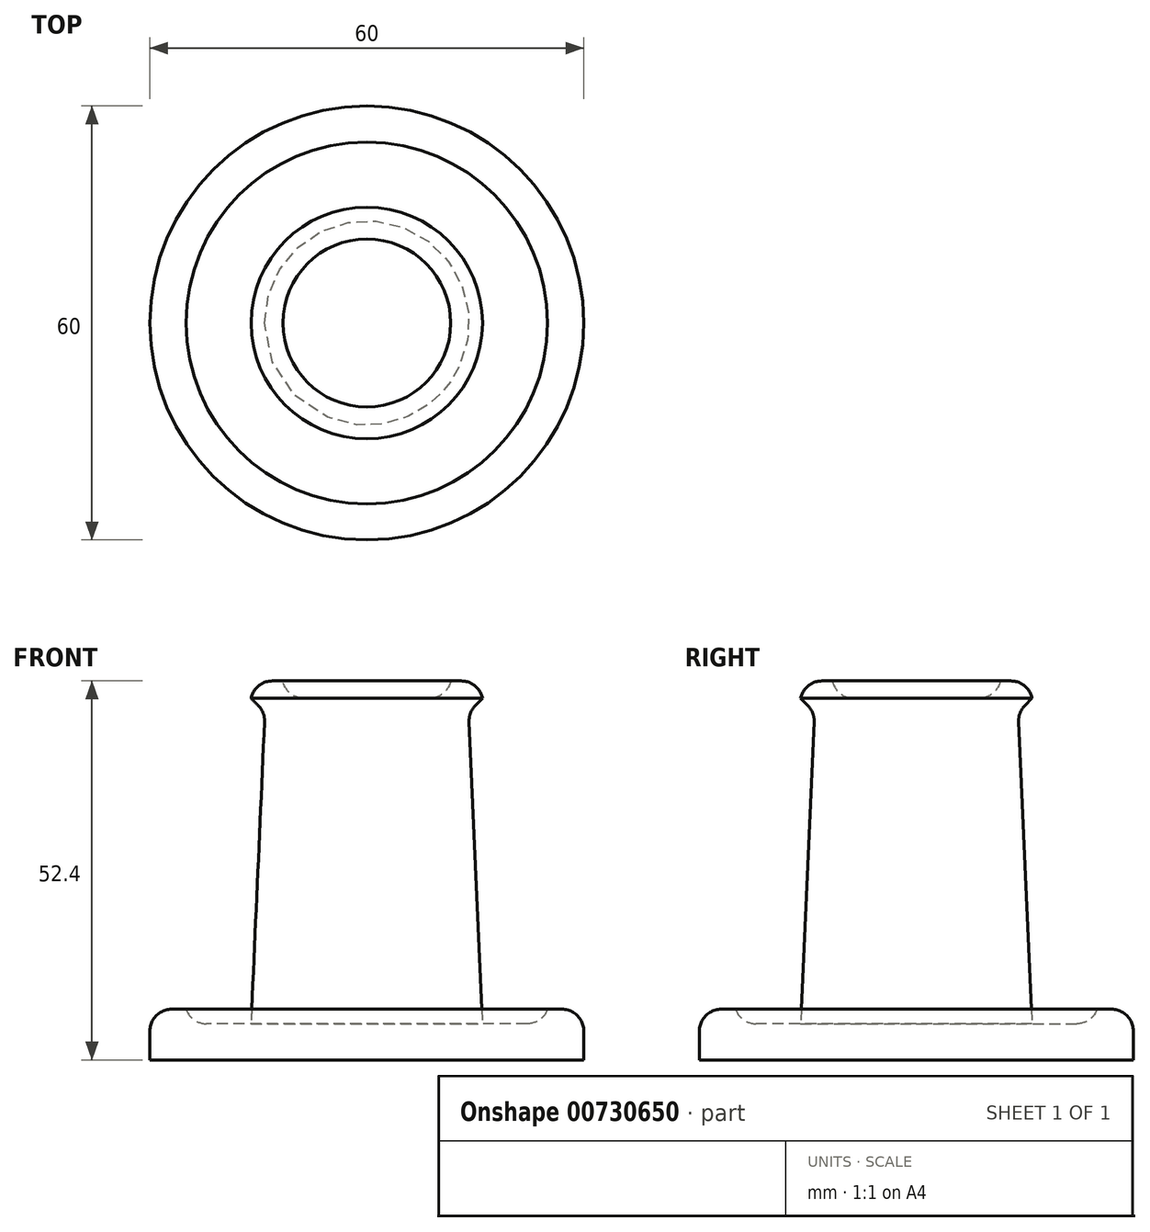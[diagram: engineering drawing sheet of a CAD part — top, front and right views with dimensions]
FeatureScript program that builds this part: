
annotation { "Feature Type Name" : "Feature", "Feature Type Description" : "" }
export const myFeature = defineFeature(function(context is Context, id is Id, definition is map)
    precondition{}
    {
        {
            var Q0;
            Q0=qCreatedBy(makeId("Front.planeOp"),FACE);
            var sketch = newSketch(context, id + "F0", { "sketchPlane" : qUnion([Q0])});
            skLineSegment(sketch, "E0", {"start": v(-30, 0) * mm, "end": v(-30, 7) * mm});
            skLineSegment(sketch, "E1", {"start": v(-30, 7) * mm, "end": v(-25, 7) * mm});
            skLineSegment(sketch, "E2", {"start": v(-25, 7) * mm, "end": v(-25, 5) * mm});
            skLineSegment(sketch, "E3", {"start": v(-25, 5) * mm, "end": v(-16, 5) * mm});
            skLineSegment(sketch, "E4", {"start": v(-16, 5) * mm, "end": v(-14.09, 48.09) * mm});
            skLineSegment(sketch, "E5", {"start": v(-14, 50) * mm, "end": v(-11.6, 50) * mm, "construction": true});
            skLineSegment(sketch, "E6", {"start": v(0, 50) * mm, "end": v(0, 0) * mm});
            skLineSegment(sketch, "E7", {"start": v(0, 0) * mm, "end": v(-30, 0) * mm});
            skLineSegment(sketch, "E8", {"start": v(0, -33) * mm, "end": v(0, 64.71) * mm, "construction": true});
            skPoint(sketch, "E9", {"position": v(0, 15.86) * mm});
            skLineSegment(sketch, "E10", {"start": v(-16, 5) * mm, "end": v(-16, 80.22) * mm, "construction": true});
            skLineSegment(sketch, "E11", {"start": v(-14, 50) * mm, "end": v(-16, 50) * mm, "construction": true});
            skLineSegment(sketch, "E12", {"start": v(-16, 50) * mm, "end": v(-14.09, 48.09) * mm});
            skLineSegment(sketch, "E13", {"start": v(-16, 50) * mm, "end": v(-16, 52.4) * mm});
            skLineSegment(sketch, "E14", {"start": v(-16, 52.4) * mm, "end": v(-11.6, 52.4) * mm});
            skLineSegment(sketch, "E15", {"start": v(-11.6, 52.4) * mm, "end": v(-11.6, 50) * mm});
            skLineSegment(sketch, "E16", {"start": v(0, 50) * mm, "end": v(-11.6, 50) * mm});
            skSolve(sketch);
        }
        {
            var Q0;
            Q0 = qSketchRegion(id + "F0", true);
            var Q1;
            Q1=sQuery(id+"F0.wireOp",EDGE,"E8");
            revolve(context, id + "F1", {"surfaceOperationType" : NewSurfaceOperationType.NEW, "entities" : qUnion([Q0]), "axis" : qUnion([Q1]), "revolveType" : RevolveType.FULL});
        }
        {
            var Q0;
            Q0=makeQuery(id+"F1.opRevolve","SWEPT_EDGE",EDGE,{"disambiguationData":[OSD([sQuery(id+"F0.wireOp",EDGE,"E2"),sQuery(id+"F0.wireOp",EDGE,"E3")])]});
            var Q1;
            Q1=makeQuery(id+"F1.opRevolve","SWEPT_EDGE",EDGE,{"disambiguationData":[OSD([sQuery(id+"F0.wireOp",EDGE,"E0"),sQuery(id+"F0.wireOp",EDGE,"E1")])]});
            var Q2;
            Q2=makeQuery(id+"F1.opRevolve","SWEPT_EDGE",EDGE,{"disambiguationData":[OSD([sQuery(id+"F0.wireOp",EDGE,"E4"),sQuery(id+"F0.wireOp",EDGE,"E12")])]});
            var Q3;
            Q3=makeQuery(id+"F1.opRevolve","SWEPT_EDGE",EDGE,{"disambiguationData":[OSD([sQuery(id+"F0.wireOp",EDGE,"E13"),sQuery(id+"F0.wireOp",EDGE,"E14")])]});
            var Q4;
            Q4=makeQuery(id+"F1.opRevolve","SWEPT_EDGE",EDGE,{"disambiguationData":[OSD([sQuery(id+"F0.wireOp",EDGE,"E15"),sQuery(id+"F0.wireOp",EDGE,"E16")])]});
            fillet(context, id + "F2", {"entities" : qUnion([Q0, Q1, Q2, Q3, Q4]), "tangentPropagation" : true, "radius" : 3 * mm, "defaultsChanged" : false, "vertexSettings" : [], "allowEdgeOverflow" : false});
        }
    });
